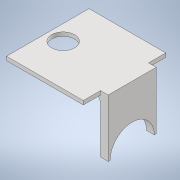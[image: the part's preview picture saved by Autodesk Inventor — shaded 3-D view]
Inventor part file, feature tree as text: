
AUTODESK INVENTOR PART (.ipt)
format: ipt  version: 2022.3 (Build 263350000, 350)  size: 144,896 bytes
history: native  units: mm
features: extrude x4, sketch x4, fillet x1
ambient origin geometry x8: Origin, YZ Plane, XZ Plane, XY Plane, X Axis, Y Axis, Z Axis, Center Point
bodies: Solid1 (feature_tree)
feature tree (9):
  extrude  "Extrusion1"  Depth=43.0mm
  extrude  "Extrusion3"  Depth=4.0mm
  extrude  "Extrusion4"  Depth=4.0mm
  extrude  "Extrusion5"  Depth=30.0mm TaperAngle=0.0deg
  fillet  "Fillet1"  Radius=23.0mm
  sketch  "Sketch1"  dims[d0=44.0mm d1=43.0mm]
  sketch  "Sketch3"  dims[d2=2.0mm d3=0.0mm d7=4.0mm]
  sketch  "Sketch4"  dims[d8=9.0mm d9=4.0mm]
  sketch  "Sketch5"  dims[d10=9.0mm d11=30.0mm d12=0.0mm d13=23.0mm d14=4.0mm d15=0.0mm d16=8.0mm d17=0.0mm d18=12.0mm d19=0.0mm d20=0.0mm d21=4.0mm]
